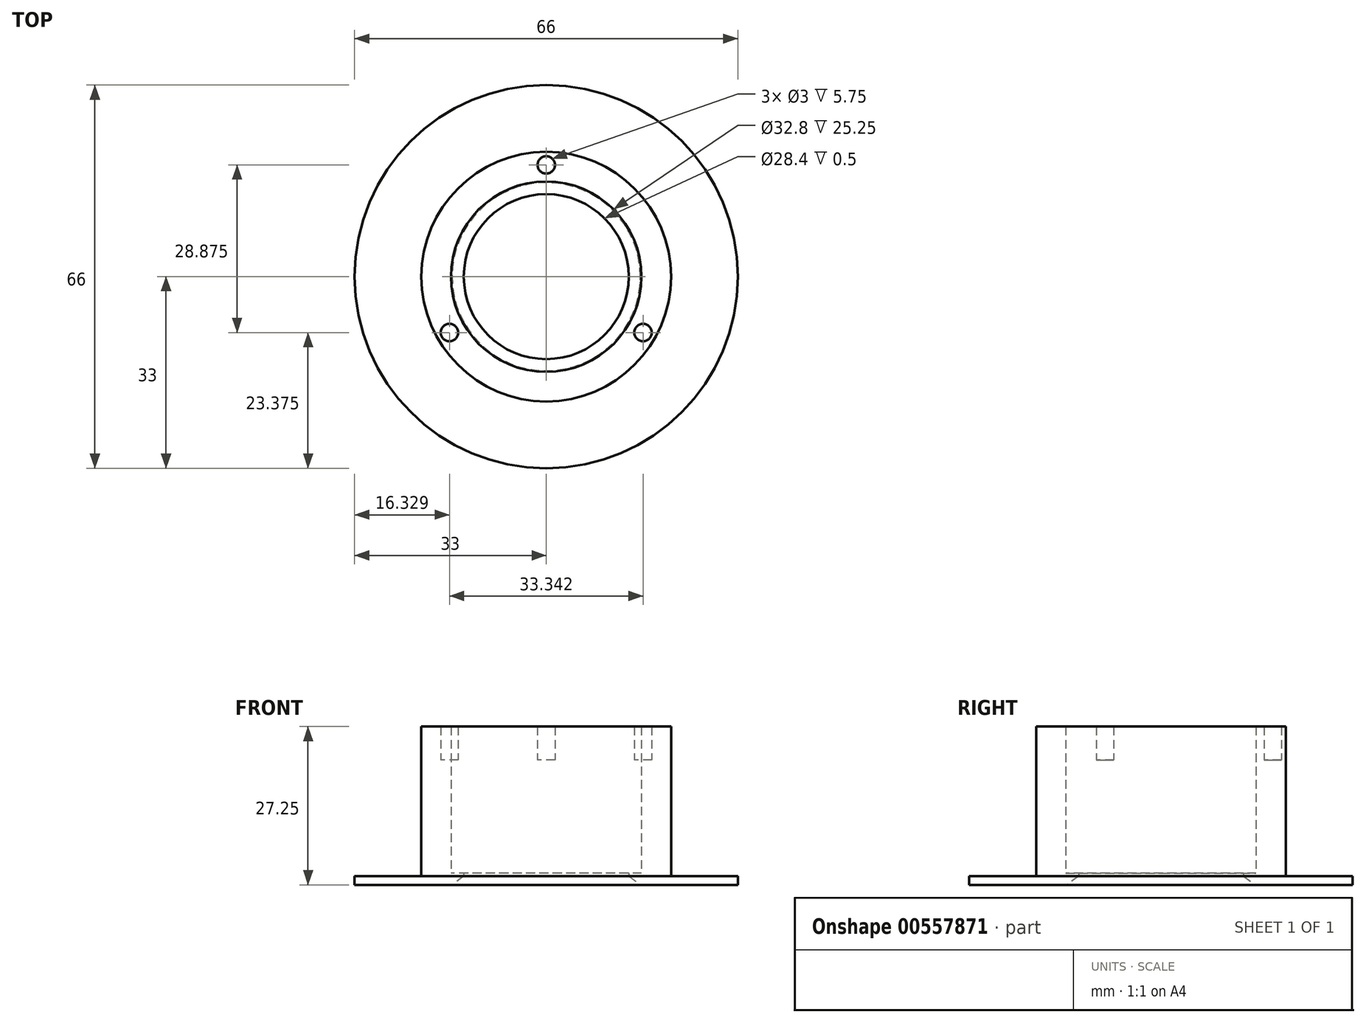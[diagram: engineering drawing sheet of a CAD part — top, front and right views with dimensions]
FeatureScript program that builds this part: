
annotation { "Feature Type Name" : "Feature", "Feature Type Description" : "" }
export const myFeature = defineFeature(function(context is Context, id is Id, definition is map)
    precondition{}
    {
        {
            var Q0;
            Q0=qCreatedBy(makeId("Top.planeOp"),FACE);
            var sketch = newSketch(context, id + "F0", { "sketchPlane" : qUnion([Q0])});
            skCircle(sketch, "E0", {"center": v(0, 0) * mm, "radius": 19.25 * mm});
            skCircle(sketch, "E1", {"center": v(0, 19.25) * mm, "radius": 1.5 * mm});
            skCircle(sketch, "E2.1.0", {"center": v(-16.67, -9.62) * mm, "radius": 1.5 * mm});
            skCircle(sketch, "E2.2.0", {"center": v(16.67, -9.62) * mm, "radius": 1.5 * mm});
            skCircle(sketch, "E3", {"center": v(0, 0) * mm, "radius": 21.5 * mm});
            skCircle(sketch, "E4", {"center": v(0, 0) * mm, "radius": 16.4 * mm});
            skCircle(sketch, "E5", {"center": v(0, 0) * mm, "radius": 14.2 * mm});
            skCircle(sketch, "E6", {"center": v(0, 0) * mm, "radius": 33 * mm});
            skSolve(sketch);
        }
        {
            var Q0;
            Q0 = qSketchRegion(id + "F0", true);
            extrude(context, id + "F1", {"entities" : qUnion([Q0]), "depth" : 1.5 * mm, "offsetDistance" : 25 * mm});
        }
        {
            var Q0;
            Q0=makeQuery(id+"F0.imprint","IMPRINT",FACE,{"disambiguationData":[TD([[makeQuery(id+"F0.imprint","IMPRINT",EDGE,{"derivedFrom":sQuery(id+"F0.wireOp",EDGE,"E3")}),1.0]])]});
            var Q1;
            Q1=makeQuery(id+"F0.imprint","IMPRINT",FACE,{"disambiguationData":[TD([[makeQuery(id+"F0.imprint","IMPRINT",EDGE,{"derivedFrom":sQuery(id+"F0.wireOp",EDGE,"E4")}),-1.0]])]});
            extrude(context, id + "F2", {"entities" : qUnion([Q0, Q1]), "operationType" : NewBodyOperationType.ADD, "depth" : 27.25 * mm, "offsetDistance" : 25 * mm});
        }
        {
            var Q0;
            Q0=makeQuery(id+"F0.imprint","IMPRINT",FACE,{"disambiguationData":[TD([[makeQuery(id+"F0.imprint","IMPRINT",EDGE,{"derivedFrom":sQuery(id+"F0.wireOp",EDGE,"E4")}),1.0]])]});
            extrude(context, id + "F3", {"entities" : qUnion([Q0]), "operationType" : NewBodyOperationType.ADD, "depth" : 2 * mm, "offsetDistance" : 25 * mm});
        }
        {
            var Q0;
            {var subQ0=sQuery(id+"F0.wireOp",EDGE,"E2.1.0");var subQ1=sQuery(id+"F0.wireOp",EDGE,"E0");var subQ2=makeQuery(id+"F0.imprint","INTERSECT",VERTEX,{"disambiguationData":[OD(0.0)],"derivedFrom":[subQ1,subQ0]});Q0=makeQuery(id+"F0.imprint","IMPRINT",FACE,{"disambiguationData":[TD([[makeQuery(id+"F0.imprint","IMPRINT",EDGE,{"disambiguationData":[TD([[subQ2,-1.0]])],"derivedFrom":subQ1}),-1.0]])]});}
            var Q1;
            {var subQ0=sQuery(id+"F0.wireOp",EDGE,"E2.1.0");var subQ1=sQuery(id+"F0.wireOp",EDGE,"E0");var subQ2=makeQuery(id+"F0.imprint","INTERSECT",VERTEX,{"disambiguationData":[OD(0.0)],"derivedFrom":[subQ1,subQ0]});Q1=makeQuery(id+"F0.imprint","IMPRINT",FACE,{"disambiguationData":[TD([[makeQuery(id+"F0.imprint","IMPRINT",EDGE,{"disambiguationData":[TD([[subQ2,-1.0]])],"derivedFrom":subQ1}),1.0]])]});}
            var Q2;
            {var subQ0=sQuery(id+"F0.wireOp",EDGE,"E2.2.0");var subQ1=sQuery(id+"F0.wireOp",EDGE,"E0");var subQ2=makeQuery(id+"F0.imprint","INTERSECT",VERTEX,{"disambiguationData":[OD(0.0)],"derivedFrom":[subQ1,subQ0]});Q2=makeQuery(id+"F0.imprint","IMPRINT",FACE,{"disambiguationData":[TD([[makeQuery(id+"F0.imprint","IMPRINT",EDGE,{"disambiguationData":[TD([[subQ2,-1.0]])],"derivedFrom":subQ1}),-1.0]])]});}
            var Q3;
            {var subQ0=sQuery(id+"F0.wireOp",EDGE,"E2.2.0");var subQ1=sQuery(id+"F0.wireOp",EDGE,"E0");var subQ2=makeQuery(id+"F0.imprint","INTERSECT",VERTEX,{"disambiguationData":[OD(0.0)],"derivedFrom":[subQ1,subQ0]});Q3=makeQuery(id+"F0.imprint","IMPRINT",FACE,{"disambiguationData":[TD([[makeQuery(id+"F0.imprint","IMPRINT",EDGE,{"disambiguationData":[TD([[subQ2,-1.0]])],"derivedFrom":subQ1}),1.0]])]});}
            var Q4;
            {var subQ0=sQuery(id+"F0.wireOp",EDGE,"E1");var subQ1=sQuery(id+"F0.wireOp",EDGE,"E0");var subQ2=makeQuery(id+"F0.imprint","INTERSECT",VERTEX,{"disambiguationData":[OD(0.0)],"derivedFrom":[subQ1,subQ0]});Q4=makeQuery(id+"F0.imprint","IMPRINT",FACE,{"disambiguationData":[TD([[makeQuery(id+"F0.imprint","IMPRINT",EDGE,{"disambiguationData":[TD([[subQ2,1.0]])],"derivedFrom":subQ1}),-1.0]])]});}
            var Q5;
            {var subQ0=sQuery(id+"F0.wireOp",EDGE,"E1");var subQ1=sQuery(id+"F0.wireOp",EDGE,"E0");var subQ2=makeQuery(id+"F0.imprint","INTERSECT",VERTEX,{"disambiguationData":[OD(0.0)],"derivedFrom":[subQ1,subQ0]});Q5=makeQuery(id+"F0.imprint","IMPRINT",FACE,{"disambiguationData":[TD([[makeQuery(id+"F0.imprint","IMPRINT",EDGE,{"disambiguationData":[TD([[subQ2,1.0]])],"derivedFrom":subQ1}),1.0]])]});}
            extrude(context, id + "F4", {"entities" : qUnion([Q0, Q1, Q2, Q3, Q4, Q5]), "operationType" : NewBodyOperationType.ADD, "depth" : 21.5 * mm, "offsetDistance" : 25 * mm});
        }
        {
            var Q0;
            Q0=makeQuery(id+"F3.opExtrude","CAP_EDGE",EDGE,{"disambiguationData":[OSD([sQuery(id+"F0.wireOp",EDGE,"E5")])],"isStart":true});
            chamfer(context, id + "F5", {"entities" : qUnion([Q0]), "chamferType" : ChamferType.TWO_OFFSETS, "width1" : 2 * mm, "oppositeDirection" : false, "width2" : 1.5 * mm, "tangentPropagation" : true});
        }
    });
